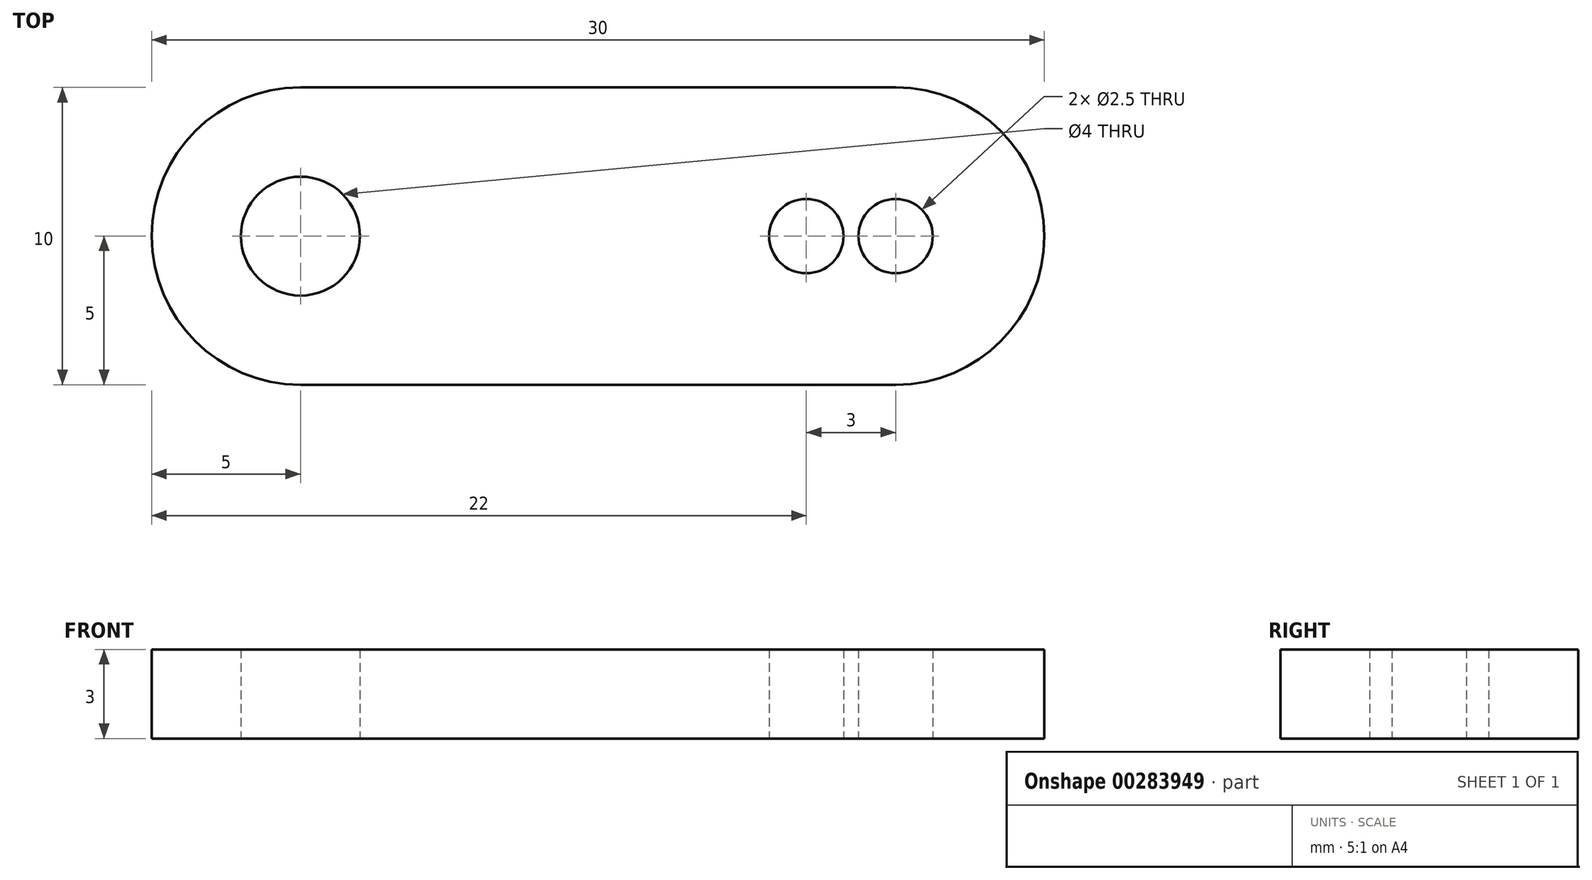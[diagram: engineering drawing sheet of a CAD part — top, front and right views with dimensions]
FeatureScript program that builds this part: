
annotation { "Feature Type Name" : "Feature", "Feature Type Description" : "" }
export const myFeature = defineFeature(function(context is Context, id is Id, definition is map)
    precondition{}
    {
        {
            var Q0;
            Q0=qCreatedBy(makeId("Top.planeOp"),FACE);
            var sketch = newSketch(context, id + "F0", { "sketchPlane" : qUnion([Q0])});
            skLineSegment(sketch, "E0.bottom", {"start": v(5, 0) * mm, "end": v(25, 0) * mm});
            skLineSegment(sketch, "E0.top", {"start": v(5, 10) * mm, "end": v(25, 10) * mm});
            skLineSegment(sketch, "E0.left", {"start": v(0, 5) * mm, "end": v(0, 5) * mm});
            skLineSegment(sketch, "E0.right", {"start": v(30, 5) * mm, "end": v(30, 5) * mm});
            skCircle(sketch, "E1", {"center": v(5, 5) * mm, "radius": 2 * mm});
            skPoint(sketch, "E1.centerSnap0", {"position": v(0, 5) * mm});
            skCircle(sketch, "E2", {"center": v(25, 5) * mm, "radius": 1.25 * mm});
            skPoint(sketch, "E2.centerSnap0", {"position": v(30, 5) * mm});
            skPoint(sketch, "E3.visualSharp", {"position": v(0, 10) * mm});
            skArc(sketch, "E3.filletArc", {"start": v(5, 10) * mm, "mid": v(1.46, 8.54) * mm, "end": v(0, 5) * mm});
            skPoint(sketch, "E4.visualSharp", {"position": v(0, 0) * mm});
            skArc(sketch, "E4.filletArc", {"start": v(0, 5) * mm, "mid": v(1.46, 1.46) * mm, "end": v(5, 0) * mm});
            skPoint(sketch, "E5.visualSharp", {"position": v(30, 0) * mm});
            skArc(sketch, "E5.filletArc", {"start": v(25, 0) * mm, "mid": v(28.54, 1.46) * mm, "end": v(30, 5) * mm});
            skPoint(sketch, "E6.visualSharp", {"position": v(30, 10) * mm});
            skArc(sketch, "E6.filletArc", {"start": v(30, 5) * mm, "mid": v(28.54, 8.54) * mm, "end": v(25, 10) * mm});
            skCircle(sketch, "E7.1.0.0", {"center": v(22, 5) * mm, "radius": 1.25 * mm});
            skLineSegment(sketch, "E7.direction1", {"start": v(25, 5) * mm, "end": v(22, 5) * mm, "construction": true});
            skSolve(sketch);
        }
        {
            var Q0;
            Q0 = qSketchRegion(id + "F0", true);
            extrude(context, id + "F1", {"entities" : qUnion([Q0]), "depth" : 3 * mm});
        }
    });
